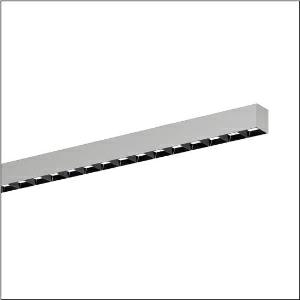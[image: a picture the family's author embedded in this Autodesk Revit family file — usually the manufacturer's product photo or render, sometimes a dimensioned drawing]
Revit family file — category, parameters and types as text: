
# Revit family: silica_21_51mx22tctas
name_source: partatom
category: Lighting Fixtures
units: mm (PartAtom-declared; Revit-internal decimal feet)

## family parameters
Cut with Voids When Loaded = No
Host = Face
Light Source = No
Part Type = Normal
Room Calculation Point = No
Round Connector Dimension = Use Diameter
Shared = No

## types (1)
- --- (1 x LED, 9300 lm, 80.4 W, 6500K)
    Apparent Load = 80 VA
    CIE Flux Codes = 84 100 100 100 100
    Color Rendering = 80
    Color Temperature = 6500K
    Default Elevation = 1800 mm
    Description = Silica 21, office luminaire, primary light control with darklight reflector, of PMMA, black, CAT 2 (L<= 3000cd/m²), light emission: direct distribution, primary light characteristic: symmetric, installation type: surface-mounted, LED, rated luminous flux: 9.300lm, luminous efficacy: 110lm/W, light colour: 8tw, colour temperature: 2700..6500K, control gear: DALI DT8, with terminal, 3+2-pole, max. 2.5mm², mains connection: 220..240V, AC, 50/60Hz, rated input power: 84.5W, luminaire housing, of aluminium, metallic grey (RAL 9006), length: 3.004mm, width: 53mm, height: 53mm, protection rating (complete): IP20, insulation class (complete): insulation class I (protective earthing), certification: CE, permissible operating ambient temperature: 0..+35°C, standard: EN 50419, packaging unit: 1 piece
    Height = 53 mm
    Lamp = 1 x LED
    Lamp Light Flux = 9300 lm
    Lamp Power = 80.4 W
    Lamp count = 1
    Length = 3004 mm
    Luminous efficacy = 116 lm/W
    Manufacturer = Siteco
    ModVariant = No
    Model = 51MX22TCTAS
    Mounting Place = Ceiling
    Mounting Type = Surface mounted
    Number of Poles = 1
    OnlyDefault = Yes
    Power Factor = 1
    Product Name = Silica 21
    Product group = office luminaire | ceiling mounted
    ProductGroupID = 301
    Protection Class = Protection class I
    Protection Degree = IP 20
    RLX_Detail_Level = 1
    RLX_Emergency_Light_Flux = 0 lm
    RLX_Emergency_Type = 0
    RLX_Emergency_Type_DB = No
    RlxData = <blob elided: 59897 chars, md5=169d4dbb>
    Socket = socket
    Standby Power = 0 W
    System Light Flux = 9300 lm
    System Power = 80 W
    Type Comments = individual setting
    Type Image = l_1335929.jpg
    URL = http://relux.com
    VarID = @adj_141163
    Voltage = 0 V
    Weight = 0.00 kg
    Width = 53 mm

## geometry (parser evidence)
native form markers: Blend x4, Sweep x11
no freeform markers — native parametric forms only
